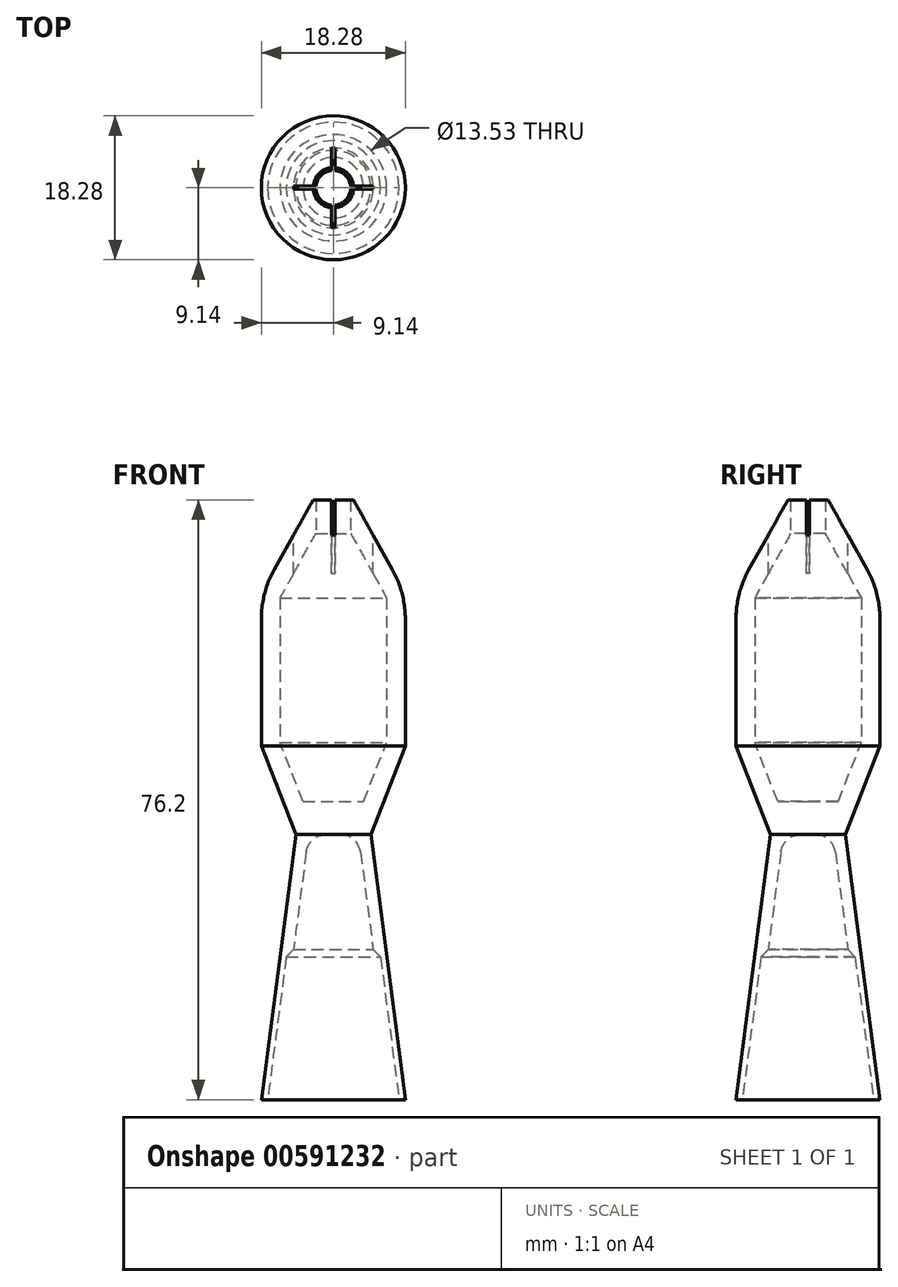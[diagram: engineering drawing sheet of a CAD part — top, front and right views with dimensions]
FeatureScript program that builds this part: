
annotation { "Feature Type Name" : "Feature", "Feature Type Description" : "" }
export const myFeature = defineFeature(function(context is Context, id is Id, definition is map)
    precondition{}
    {
        {
            var Q0;
            Q0=qCreatedBy(makeId("Front.planeOp"),FACE);
            var sketch = newSketch(context, id + "F0", { "sketchPlane" : qUnion([Q0])});
            skLineSegment(sketch, "E0", {"start": v(0, -33.67) * mm, "end": v(0, 42.53) * mm});
            skLineSegment(sketch, "E1", {"start": v(0, 42.53) * mm, "end": v(-2.57, 42.53) * mm});
            skLineSegment(sketch, "E2", {"start": v(-2.57, 42.53) * mm, "end": v(-9.14, 30.7) * mm});
            skLineSegment(sketch, "E3", {"start": v(-9.14, 30.7) * mm, "end": v(-9.14, 11.24) * mm});
            skLineSegment(sketch, "E4", {"start": v(-9.14, 11.24) * mm, "end": v(-4.76, 0) * mm});
            skLineSegment(sketch, "E5", {"start": v(-4.76, 0) * mm, "end": v(-9.14, -33.67) * mm});
            skLineSegment(sketch, "E6", {"start": v(-9.14, -33.67) * mm, "end": v(0, -33.67) * mm});
            skSolve(sketch);
        }
        {
            var Q0;
            Q0 = qSketchRegion(id + "F0", true);
            var Q1;
            Q1=sQuery(id+"F0.wireOp",EDGE,"E0");
            revolve(context, id + "F1", {"surfaceOperationType" : NewSurfaceOperationType.NEW, "entities" : qUnion([Q0]), "axis" : qUnion([Q1]), "revolveType" : RevolveType.FULL});
        }
        {
            var Q0;
            Q0=makeQuery(id+"F1.opRevolve","SWEPT_EDGE",EDGE,{"disambiguationData":[OSD([sQuery(id+"F0.wireOp",EDGE,"E2"),sQuery(id+"F0.wireOp",EDGE,"E3")])]});
            fillet(context, id + "F2", {"entities" : qUnion([Q0]), "radius" : 12.7 * mm, "tangentPropagation" : true, "allowEdgeOverflow" : false});
        }
        {
            var Q0;
            Q0=qCreatedBy(makeId("Front.planeOp"),FACE);
            var sketch = newSketch(context, id + "F3", { "sketchPlane" : qUnion([Q0])});
            skLineSegment(sketch, "E7", {"start": v(0, 0) * mm, "end": v(0, -36.22) * mm});
            skLineSegment(sketch, "E8", {"start": v(0, -36.22) * mm, "end": v(-7.87, -36.22) * mm});
            skLineSegment(sketch, "E9", {"start": v(-7.87, -36.22) * mm, "end": v(-3.16, 0) * mm});
            skLineSegment(sketch, "E10", {"start": v(-3.16, 0) * mm, "end": v(0, 0) * mm});
            skLineSegment(sketch, "E11", {"start": v(-9.14, -33.67) * mm, "end": v(-4.76, 0) * mm});
            skSolve(sketch);
        }
        {
            var Q0;
            Q0 = qSketchRegion(id + "F3", true);
            var Q1;
            Q1=sQuery(id+"F3.wireOp",EDGE,"E7");
            revolve(context, id + "F4", {"operationType" : NewBodyOperationType.REMOVE, "surfaceOperationType" : NewSurfaceOperationType.NEW, "entities" : qUnion([Q0]), "axis" : qUnion([Q1]), "revolveType" : RevolveType.FULL, "oppositeDirection" : true});
        }
        {
            var Q0;
            Q0=makeQuery(id+"F4.boolean.opBoolean","COPY",EDGE,{"derivedFrom":makeQuery(id+"F4.opRevolve","SWEPT_EDGE",EDGE,{"disambiguationData":[OSD([sQuery(id+"F3.wireOp",EDGE,"E9"),sQuery(id+"F3.wireOp",EDGE,"E10")])]})});
            fillet(context, id + "F5", {"entities" : qUnion([Q0]), "radius" : 2.54 * mm, "tangentPropagation" : true, "allowEdgeOverflow" : false});
        }
        {
            var Q0;
            Q0=qCreatedBy(makeId("Front.planeOp"),FACE);
            var sketch = newSketch(context, id + "F6", { "sketchPlane" : qUnion([Q0])});
            skLineSegment(sketch, "E12", {"start": v(0, 0) * mm, "end": v(0, -36.18) * mm});
            skLineSegment(sketch, "E13", {"start": v(0, -36.18) * mm, "end": v(-8.67, -36.18) * mm});
            skLineSegment(sketch, "E14", {"start": v(-8.67, -36.18) * mm, "end": v(-5.99, -15.56) * mm});
            skLineSegment(sketch, "E15", {"start": v(-5.99, -15.56) * mm, "end": v(-3.19, -12.63) * mm});
            skLineSegment(sketch, "E16", {"start": v(-3.19, -12.63) * mm, "end": v(0, 0) * mm});
            skLineSegment(sketch, "E17", {"start": v(-9.14, -33.67) * mm, "end": v(-4.76, 0) * mm});
            skSolve(sketch);
        }
        {
            var Q0;
            Q0 = qSketchRegion(id + "F6", true);
            var Q1;
            Q1=sQuery(id+"F6.wireOp",EDGE,"E12");
            revolve(context, id + "F7", {"operationType" : NewBodyOperationType.REMOVE, "surfaceOperationType" : NewSurfaceOperationType.NEW, "entities" : qUnion([Q0]), "axis" : qUnion([Q1]), "revolveType" : RevolveType.FULL, "oppositeDirection" : true});
        }
        {
            var Q0;
            Q0=qCreatedBy(makeId("Front.planeOp"),FACE);
            var sketch = newSketch(context, id + "F8", { "sketchPlane" : qUnion([Q0])});
            skLineSegment(sketch, "E18", {"start": v(-7.54, 33.59) * mm, "end": v(-2.22, 43.15) * mm});
            skLineSegment(sketch, "E19", {"start": v(-9.14, 11.7) * mm, "end": v(-9.14, 27.41) * mm});
            skLineSegment(sketch, "E20", {"start": v(-4.76, 0) * mm, "end": v(-9.32, 11.7) * mm});
            skLineSegment(sketch, "E21", {"start": v(0, 46.77) * mm, "end": v(0, 4.2) * mm});
            skLineSegment(sketch, "E22", {"start": v(-6.76, 11.7) * mm, "end": v(-6.76, 30.1) * mm});
            skLineSegment(sketch, "E23", {"start": v(-6.76, 30.1) * mm, "end": v(-2.22, 38.26) * mm});
            skLineSegment(sketch, "E24", {"start": v(-2.22, 38.26) * mm, "end": v(-2.22, 43.15) * mm});
            skLineSegment(sketch, "E25", {"start": v(-2.22, 43.15) * mm, "end": v(0, 46.77) * mm});
            skLineSegment(sketch, "E26", {"start": v(-6.76, 11.7) * mm, "end": v(-3.85, 4.2) * mm});
            skLineSegment(sketch, "E27", {"start": v(-3.85, 4.2) * mm, "end": v(0, 4.2) * mm});
            skSolve(sketch);
        }
        {
            var Q0;
            Q0 = qSketchRegion(id + "F8", true);
            var Q1;
            Q1=sQuery(id+"F8.wireOp",EDGE,"E21");
            revolve(context, id + "F9", {"operationType" : NewBodyOperationType.REMOVE, "surfaceOperationType" : NewSurfaceOperationType.NEW, "entities" : qUnion([Q0]), "axis" : qUnion([Q1]), "revolveType" : RevolveType.FULL, "oppositeDirection" : true});
        }
        {
            var Q0;
            Q0=makeQuery(id+"F1.opRevolve","SWEPT_FACE",FACE,{"disambiguationData":[OSD([sQuery(id+"F0.wireOp",EDGE,"E1")])]});
            var sketch = newSketch(context, id + "F10", { "sketchPlane" : qUnion([Q0])});
            skLineSegment(sketch, "E28.bottom", {"start": v(-0.2, 5.05) * mm, "end": v(0.2, 5.05) * mm});
            skLineSegment(sketch, "E28.top", {"start": v(-0.2, -5.05) * mm, "end": v(0.2, -5.05) * mm});
            skLineSegment(sketch, "E28.left", {"start": v(-0.2, 5.05) * mm, "end": v(-0.2, -5.05) * mm});
            skLineSegment(sketch, "E28.right", {"start": v(0.2, 5.05) * mm, "end": v(0.2, -5.05) * mm});
            skPoint(sketch, "E29", {"position": v(0, 5.05) * mm});
            skPoint(sketch, "E30", {"position": v(0, -5.05) * mm});
            skPoint(sketch, "E31", {"position": v(0.2, 0) * mm});
            skLineSegment(sketch, "E32.bottom", {"start": v(-5.05, 0.2) * mm, "end": v(5.05, 0.2) * mm});
            skLineSegment(sketch, "E32.top", {"start": v(-5.05, -0.2) * mm, "end": v(5.05, -0.2) * mm});
            skLineSegment(sketch, "E32.left", {"start": v(-5.05, 0.2) * mm, "end": v(-5.05, -0.2) * mm});
            skLineSegment(sketch, "E32.right", {"start": v(5.05, 0.2) * mm, "end": v(5.05, -0.2) * mm});
            skPoint(sketch, "E33", {"position": v(0, 0.2) * mm});
            skPoint(sketch, "E34", {"position": v(0, -0.2) * mm});
            skPoint(sketch, "E35", {"position": v(-5.05, 0) * mm});
            skPoint(sketch, "E36", {"position": v(5.05, 0) * mm});
            skSolve(sketch);
        }
        {
            var Q0;
            Q0 = qSketchRegion(id + "F10", true);
            extrude(context, id + "F11", {"entities" : qUnion([Q0]), "operationType" : NewBodyOperationType.REMOVE, "oppositeDirection" : true, "depth" : 12.7 * mm, "offsetDistance" : 25.4 * mm});
        }
    });
